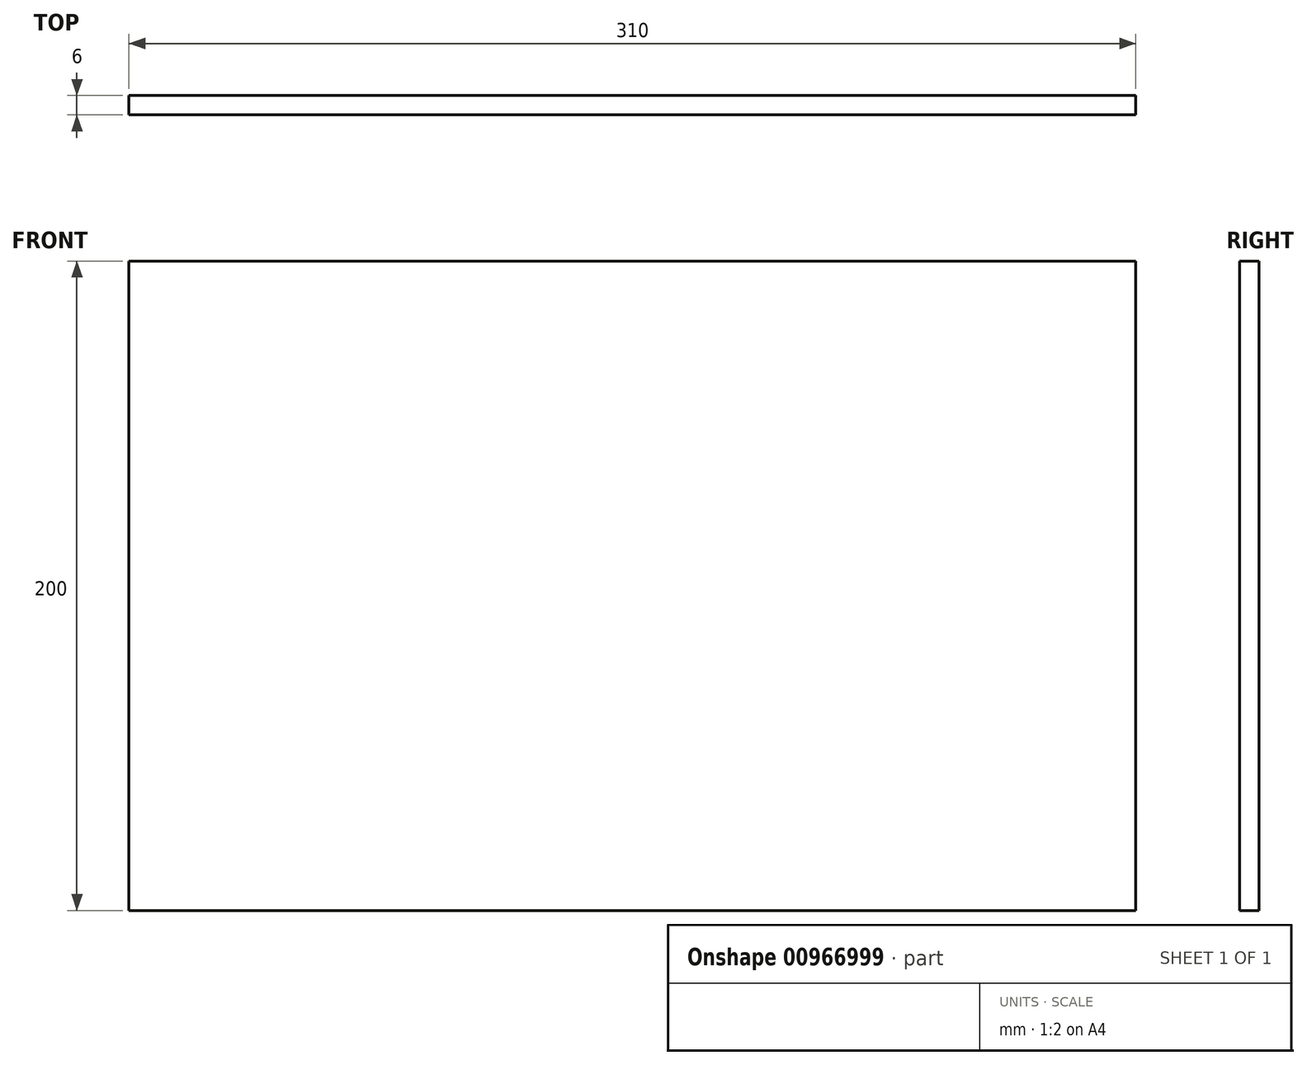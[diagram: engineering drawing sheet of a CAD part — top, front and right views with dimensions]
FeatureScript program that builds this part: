
annotation { "Feature Type Name" : "Feature", "Feature Type Description" : "" }
export const myFeature = defineFeature(function(context is Context, id is Id, definition is map)
    precondition{}
    {
        {
            var Q0;
            Q0=qCreatedBy(makeId("Front.planeOp"),FACE);
            var sketch = newSketch(context, id + "F0", { "sketchPlane" : qUnion([Q0])});
            skLineSegment(sketch, "E0.bottom", {"start": v(-155, 0) * mm, "end": v(155, 0) * mm});
            skLineSegment(sketch, "E0.top", {"start": v(-155, 200) * mm, "end": v(155, 200) * mm});
            skLineSegment(sketch, "E0.left", {"start": v(-155, 0) * mm, "end": v(-155, 200) * mm});
            skLineSegment(sketch, "E0.right", {"start": v(155, 0) * mm, "end": v(155, 200) * mm});
            skSolve(sketch);
        }
        {
            var Q0;
            Q0 = qSketchRegion(id + "F0", true);
            extrude(context, id + "F1", {"entities" : qUnion([Q0]), "oppositeDirection" : true, "depth" : 6 * mm, "offsetDistance" : 25 * mm});
        }
    });
